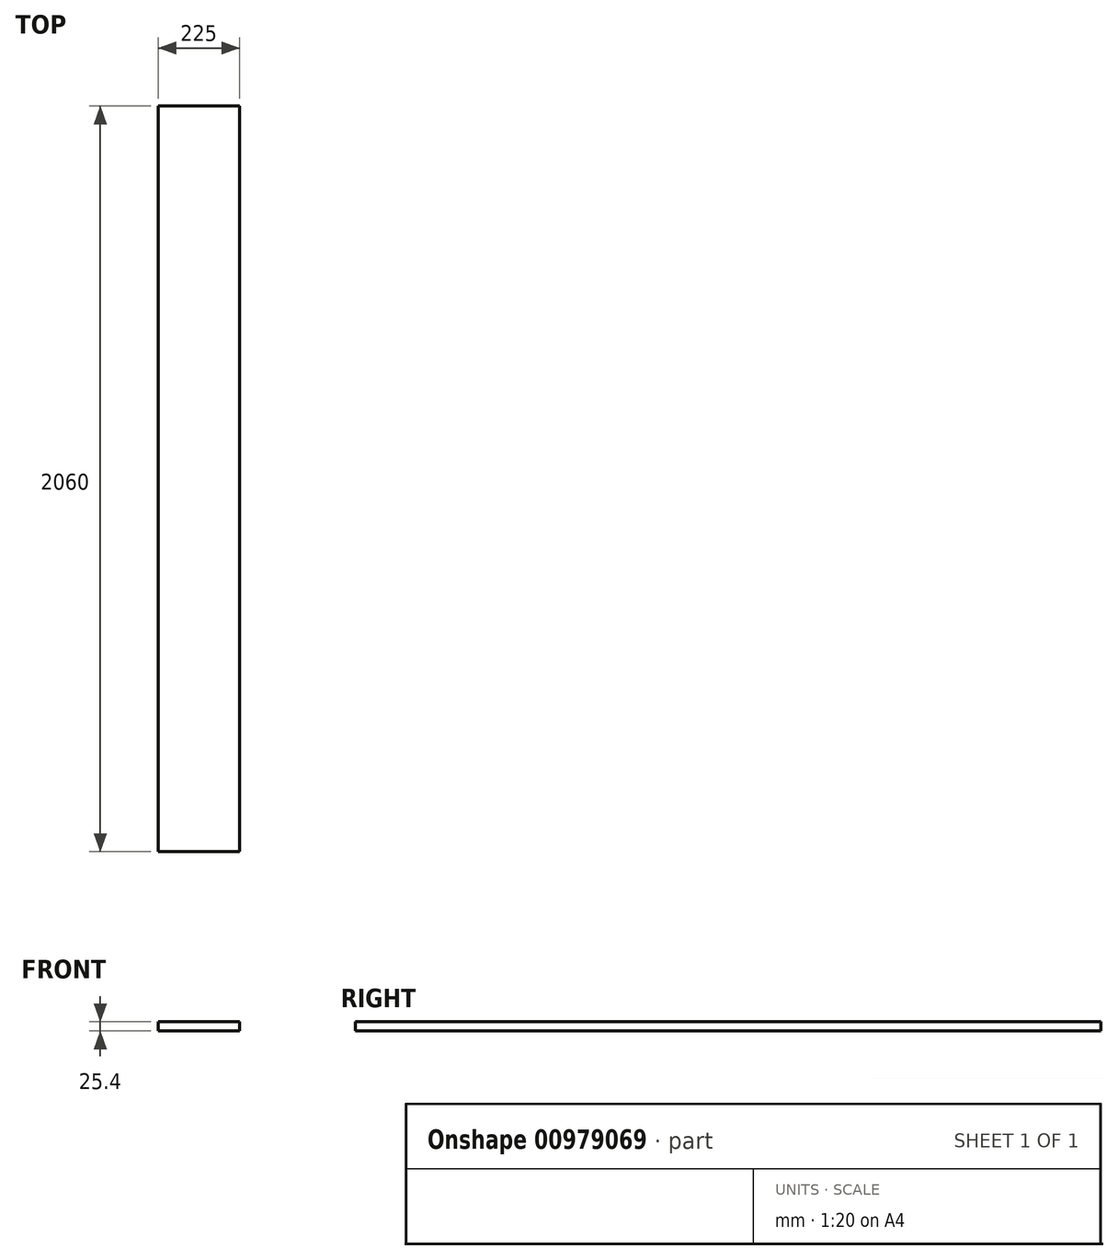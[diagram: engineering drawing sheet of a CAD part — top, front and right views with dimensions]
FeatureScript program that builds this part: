
annotation { "Feature Type Name" : "Feature", "Feature Type Description" : "" }
export const myFeature = defineFeature(function(context is Context, id is Id, definition is map)
    precondition{}
    {
        {
            var Q0;
            Q0=qCreatedBy(makeId("Top.planeOp"),FACE);
            var sketch = newSketch(context, id + "F0", { "sketchPlane" : qUnion([Q0])});
            skLineSegment(sketch, "E0.bottom", {"start": v(0, 0) * mm, "end": v(225, 0) * mm});
            skLineSegment(sketch, "E0.top", {"start": v(0, 2060) * mm, "end": v(225, 2060) * mm});
            skLineSegment(sketch, "E0.left", {"start": v(0, 0) * mm, "end": v(0, 2060) * mm});
            skLineSegment(sketch, "E0.right", {"start": v(225, 0) * mm, "end": v(225, 2060) * mm});
            skSolve(sketch);
        }
        {
            var Q0;
            Q0 = qSketchRegion(id + "F0", true);
            extrude(context, id + "F1", {"entities" : qUnion([Q0]), "depth" : 25.4 * mm, "offsetDistance" : 25.4 * mm});
        }
    });
